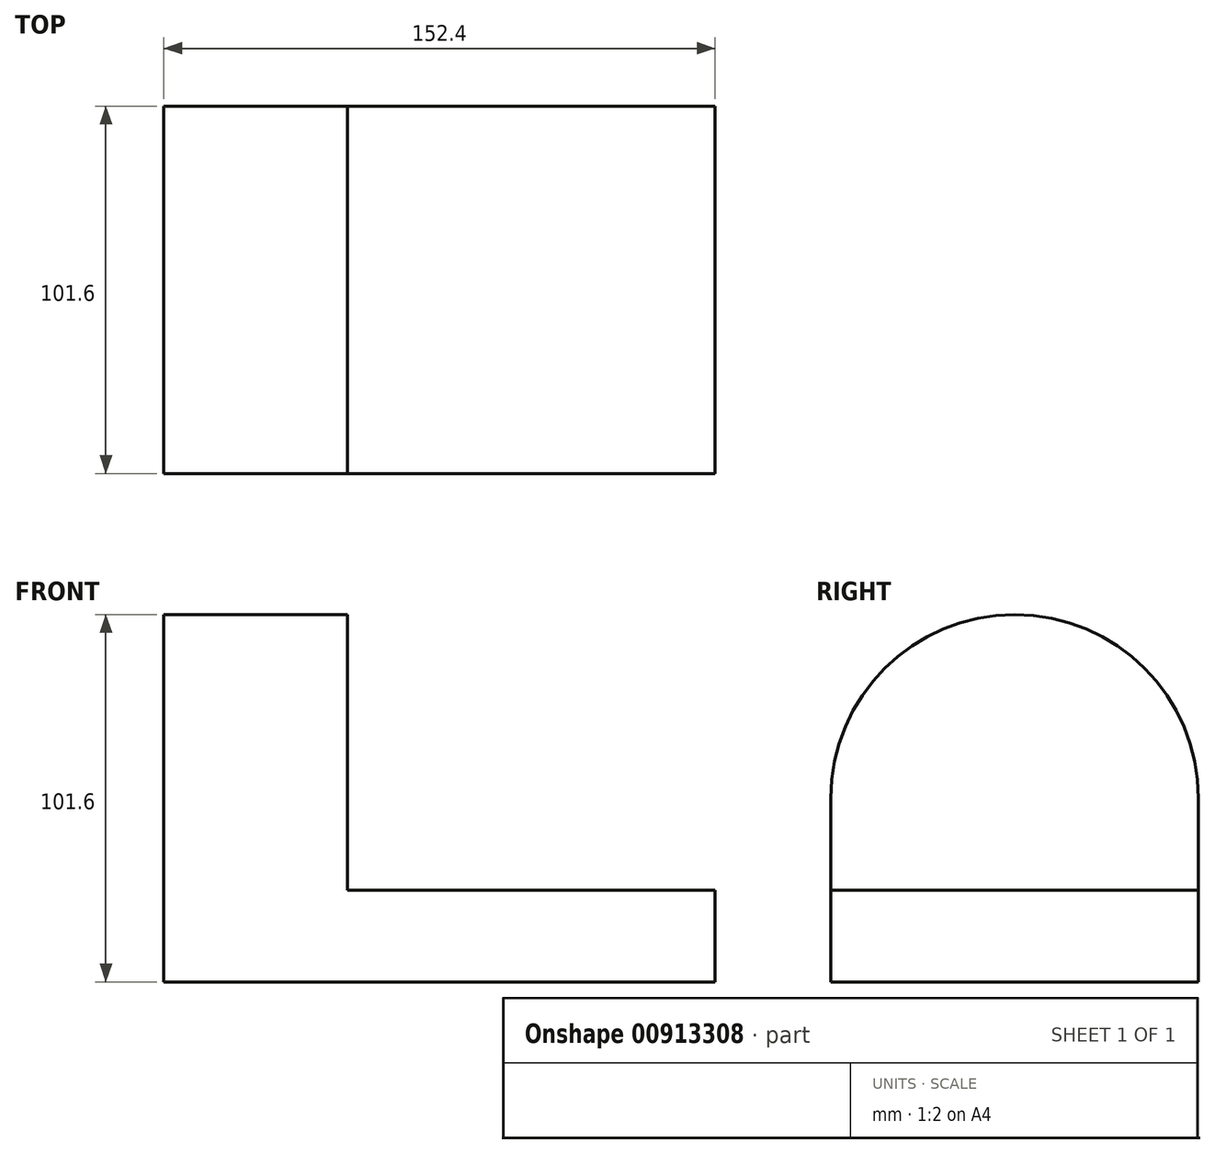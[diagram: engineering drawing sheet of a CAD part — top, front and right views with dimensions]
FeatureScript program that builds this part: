
annotation { "Feature Type Name" : "Feature", "Feature Type Description" : "" }
export const myFeature = defineFeature(function(context is Context, id is Id, definition is map)
    precondition{}
    {
        {
            var Q0;
            Q0=qCreatedBy(makeId("Top.planeOp"),FACE);
            var sketch = newSketch(context, id + "F0", { "sketchPlane" : qUnion([Q0])});
            skLineSegment(sketch, "E0.bottom", {"start": v(0, 0) * mm, "end": v(-152.4, 0) * mm});
            skLineSegment(sketch, "E0.top", {"start": v(0, 101.6) * mm, "end": v(-152.4, 101.6) * mm});
            skLineSegment(sketch, "E0.left", {"start": v(0, 0) * mm, "end": v(0, 101.6) * mm});
            skLineSegment(sketch, "E0.right", {"start": v(-152.4, 0) * mm, "end": v(-152.4, 101.6) * mm});
            skSolve(sketch);
        }
        {
            var Q0;
            Q0 = qSketchRegion(id + "F0", true);
            extrude(context, id + "F1", {"entities" : qUnion([Q0]), "depth" : 25.4 * mm, "offsetDistance" : 25.4 * mm});
        }
        {
            var Q0;
            Q0=makeQuery(id+"F1.opExtrude","SWEPT_FACE",FACE,{"disambiguationData":[OSD([sQuery(id+"F0.wireOp",EDGE,"E0.right")])]});
            var sketch = newSketch(context, id + "F2", { "sketchPlane" : qUnion([Q0])});
            skLineSegment(sketch, "E1.bottom", {"start": v(-101.6, 25.4) * mm, "end": v(0, 25.4) * mm});
            skLineSegment(sketch, "E1.top", {"start": v(-101.6, 50.8) * mm, "end": v(0, 50.8) * mm});
            skLineSegment(sketch, "E1.left", {"start": v(-101.6, 25.4) * mm, "end": v(-101.6, 50.8) * mm});
            skLineSegment(sketch, "E1.right", {"start": v(0, 25.4) * mm, "end": v(0, 50.8) * mm});
            skArc(sketch, "E2", {"start": v(0, 50.8) * mm, "mid": v(-50.8, 101.6) * mm, "end": v(-101.6, 50.8) * mm});
            skSolve(sketch);
        }
        {
            var Q0;
            Q0 = qSketchRegion(id + "F2", true);
            extrude(context, id + "F3", {"entities" : qUnion([Q0]), "operationType" : NewBodyOperationType.ADD, "oppositeDirection" : true, "depth" : 50.8 * mm, "offsetDistance" : 25.4 * mm});
        }
    });
